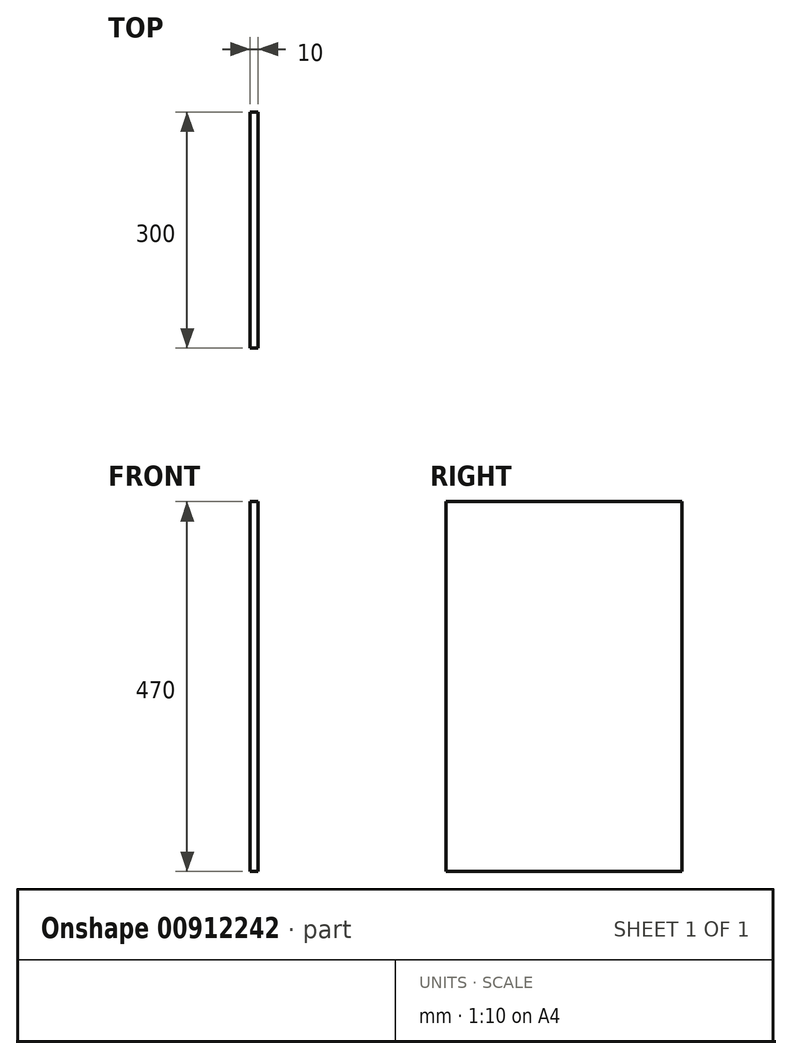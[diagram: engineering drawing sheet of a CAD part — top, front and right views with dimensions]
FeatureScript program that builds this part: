
annotation { "Feature Type Name" : "Feature", "Feature Type Description" : "" }
export const myFeature = defineFeature(function(context is Context, id is Id, definition is map)
    precondition{}
    {
        {
            var Q0;
            Q0=qCreatedBy(makeId("Right.planeOp"),FACE);
            var sketch = newSketch(context, id + "F0", { "sketchPlane" : qUnion([Q0])});
            skLineSegment(sketch, "E0.bottom", {"start": v(-203.46, 344.1) * mm, "end": v(96.54, 344.1) * mm});
            skLineSegment(sketch, "E0.top", {"start": v(-203.46, -125.9) * mm, "end": v(96.54, -125.9) * mm});
            skLineSegment(sketch, "E0.left", {"start": v(-203.46, 344.1) * mm, "end": v(-203.46, -125.9) * mm});
            skLineSegment(sketch, "E0.right", {"start": v(96.54, 344.1) * mm, "end": v(96.54, -125.9) * mm});
            skSolve(sketch);
        }
        {
            var Q0;
            Q0=makeQuery(id+"F0.imprint","IMPRINT",FACE,{"disambiguationData":[TD([[makeQuery(id+"F0.imprint","IMPRINT",EDGE,{"derivedFrom":sQuery(id+"F0.wireOp",EDGE,"E0.bottom")}),-1.0]])]});
            extrude(context, id + "F1", {"entities" : qUnion([Q0]), "depth" : 10 * mm, "offsetDistance" : 25 * mm});
        }
    });
